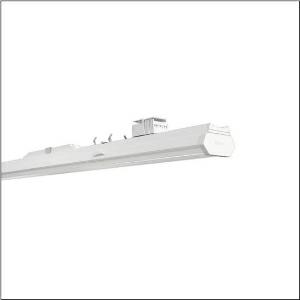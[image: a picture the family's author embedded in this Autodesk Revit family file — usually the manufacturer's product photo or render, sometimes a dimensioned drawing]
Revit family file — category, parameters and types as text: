
# Revit family: licross_r__11_protected_tw_51td1btnt8xx_5d1b
name_source: partatom
category: Lighting Fixtures
units: mm (PartAtom-declared; Revit-internal decimal feet)

## family parameters
Cut with Voids When Loaded = No
Host = Face
Light Source = No
Part Type = Normal
Room Calculation Point = No
Round Connector Dimension = Use Diameter
Shared = No

## types (1)
- --- (1 x LED 2700 K ... 6500 K, 8450 lm, 56 W, 2700K)
    Apparent Load = 56 VA
    CIE Flux Codes = 54 82 95 97 100
    Color Rendering = 80
    Color Temperature = 2700K
    Default Elevation = 1800 mm
    Description = Licross® 11 Protected TW, luminaire insert, of sheet steel, galvanised, coil coated, white, length: 1.500mm, width: 90mm, height: 101mm, LED rated luminous flux: 8.450lm, light colour: 8tw, control gear: DALI DT8, with plug, 5-pole, with phase selection, mains connection: 220..240V, AC, 50/60Hz, rated input power: 56W, internal wiring halogen-free, primary optical cover: cover, of PMMA, light emission: direct distribution, primary light characteristic: symmetric, protection rating (complete): IP54, insulation class (complete): insulation class I (protective earthing), certification: CE, ENEC, VDE, UKCA, protection symbol: D if used in an environment with non-conductive dust loads with corresponding accessories, impact resistance: IK06, permissible ambient temperature for indoor applications: -25..+35°C, corresponds to IFS (International Featured Standards) requirements for safety and quality in the food industry, reducing of maximum allowable ambient temperature of 5°C with ceiling mounting, LABS conformity tested according to VDMA 24364:2018-05, packaging unit: 1 piece
    Height = 92 mm
    Lamp = 1 x LED 2700 K ... 6500 K
    Lamp Light Flux = 8450 lm
    Lamp Power = 56 W
    Lamp count = 1
    Length = 1500 mm
    Luminous efficacy = 151 lm/W
    Manufacturer = Siteco
    ModVariant = No
    Model = 51TD1BTNT8XX
    Mounting Place = Ceiling
    Mounting Type = Pendant
    Number of Poles = 1
    OnlyDefault = Yes
    Power Factor = 1
    Product Name = Licross® 11 Protected TW
    Product group = luminaire insert | ceiling pendant
    ProductGroupID = 902
    Protection Class = Protection class I
    Protection Degree = IP 54
    RLX_Detail_Level = 1
    RLX_Emergency_Light_Flux = 0 lm
    RLX_Emergency_Type = 0
    RLX_Emergency_Type_DB = No
    RlxData = <blob elided: 20693 chars, md5=1ab94b3e>
    Socket = socket
    Standby Power = 0 W
    System Light Flux = 8450 lm
    System Power = 56 W
    Type Comments = individual setting: CCT=2700K
    Type Image = l_1256145.jpg
    URL = http://relux.com
    VarID = @adj_069853
    Voltage = 0 V
    Weight = 0.00 kg
    Width = 88 mm

## geometry (parser evidence)
native form markers: Blend x4, Sweep x12
no freeform markers — native parametric forms only
